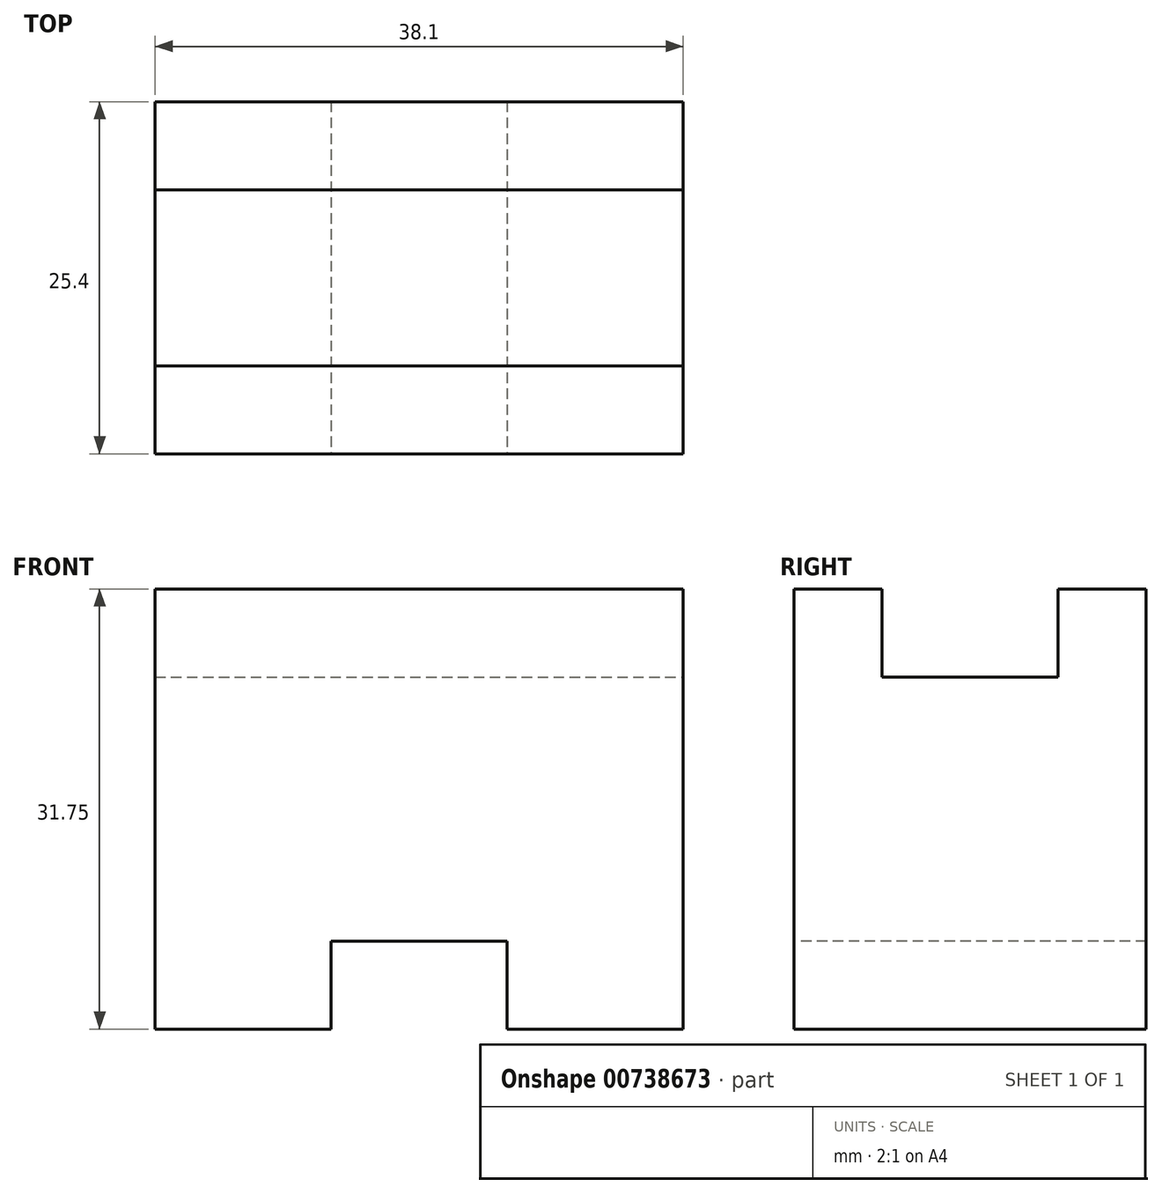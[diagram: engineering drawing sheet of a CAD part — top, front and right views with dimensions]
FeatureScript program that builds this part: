
annotation { "Feature Type Name" : "Feature", "Feature Type Description" : "" }
export const myFeature = defineFeature(function(context is Context, id is Id, definition is map)
    precondition{}
    {
        {
            var Q0;
            Q0=qCreatedBy(makeId("Front.planeOp"),FACE);
            var sketch = newSketch(context, id + "F0", { "sketchPlane" : qUnion([Q0])});
            skLineSegment(sketch, "E0", {"start": v(0, 0) * mm, "end": v(38.1, 0) * mm});
            skLineSegment(sketch, "E1", {"start": v(38.1, 0) * mm, "end": v(38.1, 31.75) * mm});
            skLineSegment(sketch, "E2", {"start": v(38.1, 31.75) * mm, "end": v(0, 31.75) * mm});
            skLineSegment(sketch, "E3", {"start": v(0, 31.75) * mm, "end": v(0, 0) * mm});
            skSolve(sketch);
        }
        {
            var Q0;
            Q0=makeQuery(id+"F0.imprint","IMPRINT",FACE,{"disambiguationData":[TD([[makeQuery(id+"F0.imprint","IMPRINT",EDGE,{"derivedFrom":sQuery(id+"F0.wireOp",EDGE,"E0")}),1.0]])]});
            extrude(context, id + "F1", {"entities" : qUnion([Q0]), "depth" : 25.4 * mm, "offsetDistance" : 25.4 * mm});
        }
        {
            var Q0;
            Q0=makeQuery(id+"F1.opExtrude","CAP_FACE",FACE,{"disambiguationData":[OSD([sQuery(id+"F0.wireOp",EDGE,"E0"),sQuery(id+"F0.wireOp",EDGE,"E1"),sQuery(id+"F0.wireOp",EDGE,"E2"),sQuery(id+"F0.wireOp",EDGE,"E3")])],"isStart":false});
            var sketch = newSketch(context, id + "F2", { "sketchPlane" : qUnion([Q0])});
            skLineSegment(sketch, "E4", {"start": v(0, 0) * mm, "end": v(12.7, 0) * mm});
            skLineSegment(sketch, "E5", {"start": v(12.7, 0) * mm, "end": v(12.7, 6.35) * mm});
            skLineSegment(sketch, "E6", {"start": v(12.7, 6.35) * mm, "end": v(25.4, 6.35) * mm});
            skLineSegment(sketch, "E7", {"start": v(25.4, 6.35) * mm, "end": v(25.4, 0) * mm});
            skLineSegment(sketch, "E8", {"start": v(25.4, 0) * mm, "end": v(38.1, 0) * mm});
            skSolve(sketch);
        }
        {
            var Q0;
            {var subQ0=sQuery(id+"F2.wireOp",EDGE,"E5");Q0=makeQuery(id+"F2.imprint","IMPRINT",FACE,{"disambiguationData":[TD([[makeQuery(id+"F2.imprint","IMPRINT",EDGE,{"derivedFrom":subQ0}),-1.0]])]});}
            extrude(context, id + "F3", {"entities" : qUnion([Q0]), "operationType" : NewBodyOperationType.REMOVE, "oppositeDirection" : true, "depth" : 25.4 * mm, "offsetDistance" : 25.4 * mm});
        }
        {
            var Q0;
            Q0=makeQuery(id+"F1.opExtrude","SWEPT_FACE",FACE,{"disambiguationData":[OSD([sQuery(id+"F0.wireOp",EDGE,"E1")])]});
            var sketch = newSketch(context, id + "F4", { "sketchPlane" : qUnion([Q0])});
            skLineSegment(sketch, "E9", {"start": v(-25.4, 31.75) * mm, "end": v(-19.05, 31.75) * mm});
            skLineSegment(sketch, "E10", {"start": v(-19.05, 31.75) * mm, "end": v(-19.05, 25.4) * mm});
            skLineSegment(sketch, "E11", {"start": v(-19.05, 25.4) * mm, "end": v(-6.35, 25.4) * mm});
            skLineSegment(sketch, "E12", {"start": v(-6.35, 25.4) * mm, "end": v(-6.35, 31.75) * mm});
            skLineSegment(sketch, "E13", {"start": v(-6.35, 31.75) * mm, "end": v(0, 31.75) * mm});
            skSolve(sketch);
        }
        {
            var Q0;
            {var subQ0=sQuery(id+"F4.wireOp",EDGE,"E10");Q0=makeQuery(id+"F4.imprint","IMPRINT",FACE,{"disambiguationData":[TD([[makeQuery(id+"F4.imprint","IMPRINT",EDGE,{"derivedFrom":subQ0}),1.0]])]});}
            extrude(context, id + "F5", {"entities" : qUnion([Q0]), "operationType" : NewBodyOperationType.REMOVE, "oppositeDirection" : true, "depth" : 38.1 * mm, "offsetDistance" : 25.4 * mm});
        }
    });
